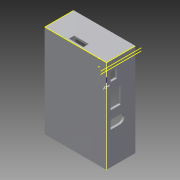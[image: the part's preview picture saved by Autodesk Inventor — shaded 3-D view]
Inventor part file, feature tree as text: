
AUTODESK INVENTOR PART (.ipt)
format: ipt  version: 2015 (Build 190159000, 159)  size: 228,864 bytes
history: native  units: mm
features: sketch x12, projected_geometry x8, extrude x6, plane x5, sweep x1
ambient origin geometry x8: Origin, YZ Plane, XZ Plane, XY Plane, X Axis, Y Axis, Z Axis, Center Point
bodies: Solid1 (feature_tree)
feature tree (32):
  sketch  "Sketch1"  dims[d0=2.5mm d1=20.0mm d3=49.0mm d4=20.0mm d6=58.0mm]
  extrude  "Extrusion1"  Depth=20.0mm
  extrude  "Extrusion2"  Depth=3.5mm
  sketch  "Sketch5"  dims[d14=3.5mm d15=2.0mm]
  sketch  "3D Sketch1"
  sweep  "Sweep2"
  extrude  "Extrusion3"  Depth=2.0mm
  extrude  "Extrusion6"  Depth=2.0mm
  sketch  "Sketch11"  dims[d25=5.0mm d26=2.0mm d27=0.0mm]
  plane  "Work Plane1"
  plane  "Work Plane2"
  sketch  "Sketch12"  dims[d44=5.0mm]
  plane  "Work Plane3"
  extrude  "Extrusion7"  TaperAngle=0.0deg  [1 undecoded]
  plane  "Work Plane5"
  extrude  "Extrusion8"  Depth=2.0mm TaperAngle=0.0deg
  sketch  "Sketch2"  dims[d9=10.0mm d10=0.0mm d11=3.5mm]
  sketch  "Sketch3"  dims[d12=27.0mm d13=3.5mm]
  projected_geometry  "Projected Loop1"
  projected_geometry  "Projected Loop2"
  projected_geometry  "Projected Loop3"
  projected_geometry  "Projected Loop4"
  sketch  "3D Sketch2"
  sketch  "Sketch6"  dims[d16=2.0mm d17=0.0mm d18=2.0mm]
  sketch  "Sketch9"  dims[d19=30.0mm d23=0.0mm d24=0.0mm]
  projected_geometry  "Projected Loop5"
  projected_geometry  "Projected Loop6"
  projected_geometry  "Projected Loop7"
  projected_geometry  "Projected Loop8"
  sketch  "Sketch13"  dims[d45=5.0mm]
  plane  "Work Plane4"
  sketch  "Sketch15"  dims[d46=5.0mm d47=5.0mm d48=4.0mm d49=0.0mm d50=0.3mm d51=0.0mm d52=0.0mm d54=1.5mm d55=9.0mm d57=10.6mm d58=32.0mm d60=17.0mm d61=1.5mm d63=9.0mm d64=53.5mm d65=1.5mm d66=9.0mm d67=5.0mm d68=10.0mm d69=0.0mm d70=-0.2mm d71=21.0mm d72=36.0mm d73=4.0mm d74=1.5mm d75=10.0mm d76=0.0mm]
note: 1 required parameter value undecoded (feature->parameter linkage not recoverable at this tier; creation-order binding heuristic only, values carry confidence <= 0.55)
